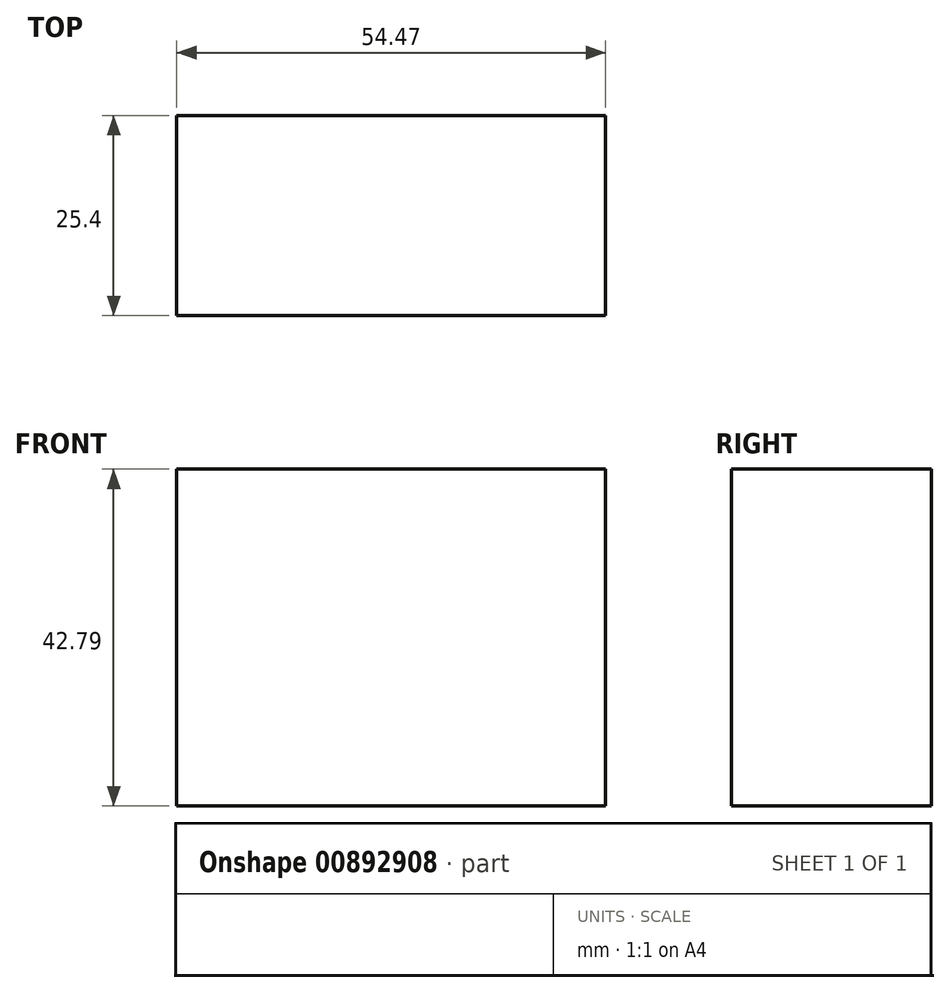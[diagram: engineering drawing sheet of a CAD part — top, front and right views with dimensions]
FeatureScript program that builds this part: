
annotation { "Feature Type Name" : "Feature", "Feature Type Description" : "" }
export const myFeature = defineFeature(function(context is Context, id is Id, definition is map)
    precondition{}
    {
        {
            var Q0;
            Q0=qCreatedBy(makeId("Front.planeOp"),FACE);
            var sketch = newSketch(context, id + "F0", { "sketchPlane" : qUnion([Q0])});
            skLineSegment(sketch, "E0.bottom", {"start": v(-102.99, 48.05) * mm, "end": v(-48.52, 48.05) * mm});
            skLineSegment(sketch, "E0.top", {"start": v(-102.99, 5.26) * mm, "end": v(-48.52, 5.26) * mm});
            skLineSegment(sketch, "E0.left", {"start": v(-102.99, 48.05) * mm, "end": v(-102.99, 5.26) * mm});
            skLineSegment(sketch, "E0.right", {"start": v(-48.52, 48.05) * mm, "end": v(-48.52, 5.26) * mm});
            skSolve(sketch);
        }
        {
            var Q0;
            Q0 = qSketchRegion(id + "F0", true);
            extrude(context, id + "F1", {"entities" : qUnion([Q0]), "depth" : 25.4 * mm, "offsetDistance" : 25.4 * mm});
        }
    });
